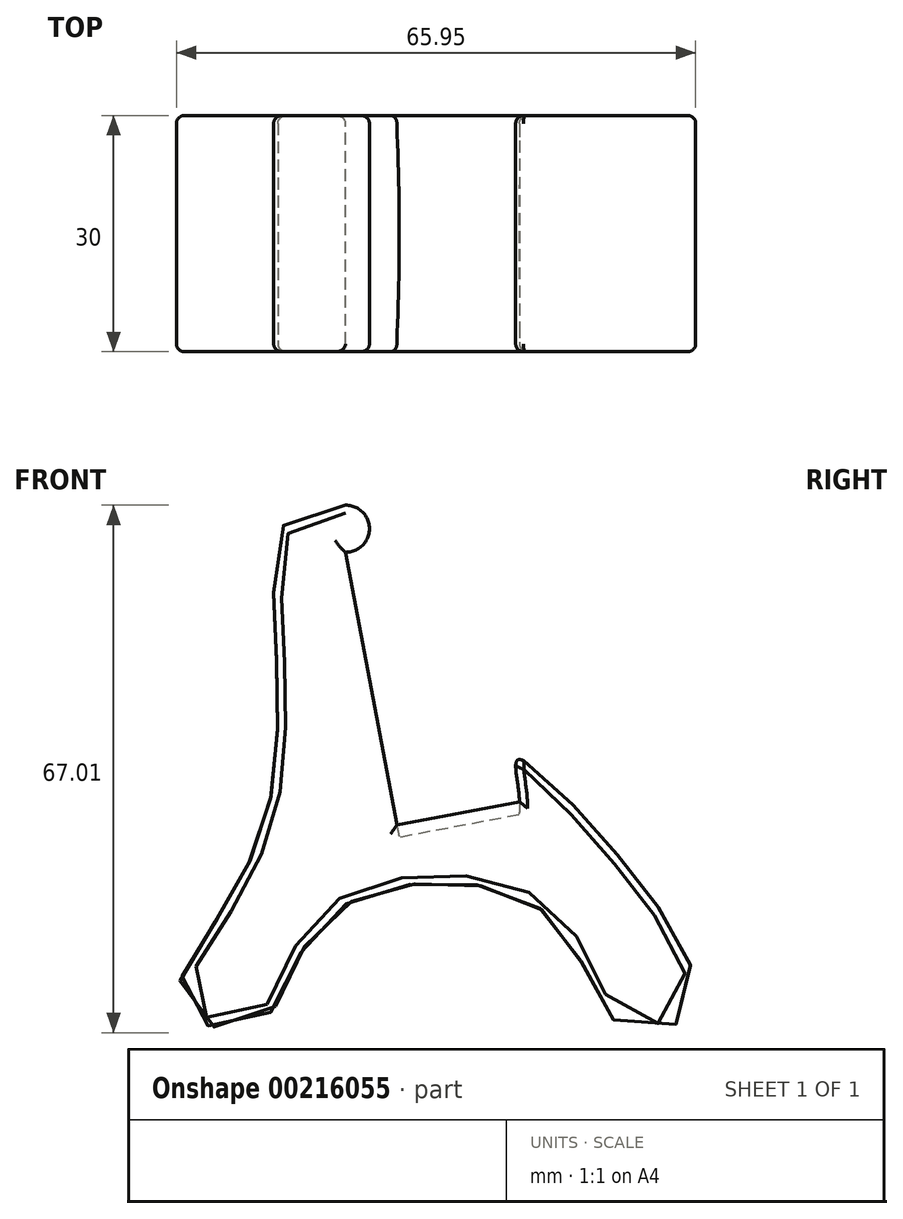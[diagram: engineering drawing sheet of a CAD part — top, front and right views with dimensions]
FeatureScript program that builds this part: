
annotation { "Feature Type Name" : "Feature", "Feature Type Description" : "" }
export const myFeature = defineFeature(function(context is Context, id is Id, definition is map)
    precondition{}
    {
        {
            var Q0;
            Q0=qCreatedBy(makeId("Front.planeOp"),FACE);
            var sketch = newSketch(context, id + "F0", { "sketchPlane" : qUnion([Q0])});
            skLineSegment(sketch, "E0", {"start": v(0, 0) * mm, "end": v(-14.9, -1.77) * mm});
            skLineSegment(sketch, "E1", {"start": v(-14.9, -1.77) * mm, "end": v(-21.73, 34.55) * mm});
            skArc(sketch, "E2", {"start": v(-21.73, 34.55) * mm, "mid": v(-18.7, 37.54) * mm, "end": v(-21.73, 40.53) * mm});
            skFitSpline(sketch, "E3", {"points": [v(-21.73, 40.53) * mm, v(-29.85, 37.54) * mm, v(-32.05, 0) * mm, v(-42.94, -23.18) * mm, v(-32.47, -24.89) * mm, v(-24.14, -11.86) * mm, v(3.42, -11) * mm, v(13.46, -25.74) * mm, v(22.43, -22.97) * mm, v(9.4, 0) * mm, v(0, 8.01) * mm, v(0, 0) * mm], "startDerivative": vector(-163.14, -3.83) * mm, "endDerivative": vector(-51.87, -133.13) * mm});
            skSolve(sketch);
        }
        {
            var Q0;
            Q0 = qSketchRegion(id + "F0", true);
            extrude(context, id + "F1", {"entities" : qUnion([Q0]), "depth" : 30 * mm});
        }
        {
            var Q0;
            Q0=makeQuery(id+"F1.opExtrude","SWEPT_FACE",FACE,{"disambiguationData":[OSD([sQuery(id+"F0.wireOp",EDGE,"E1")])]});
            var sketch = newSketch(context, id + "F2", { "sketchPlane" : qUnion([Q0])});
            skArc(sketch, "E4", {"start": v(-30, 3.01) * mm, "mid": v(-15, 1.1) * mm, "end": v(0, 3.01) * mm});
            skLineSegment(sketch, "E5", {"start": v(-30, 3.01) * mm, "end": v(-30, 1.01) * mm});
            skLineSegment(sketch, "E6", {"start": v(-30, 1.01) * mm, "end": v(0, 1.01) * mm});
            skLineSegment(sketch, "E7", {"start": v(0, 1.01) * mm, "end": v(0, 3.01) * mm});
            skSolve(sketch);
        }
        {
            var Q0;
            Q0 = qSketchRegion(id + "F2", true);
            extrude(context, id + "F3", {"entities" : qUnion([Q0]), "operationType" : NewBodyOperationType.ADD, "depth" : 18 * mm});
        }
        {
            var Q0;
            Q0=makeQuery(id+"F3.opExtrude","SWEPT_FACE",FACE,{"disambiguationData":[OSD([sQuery(id+"F2.wireOp",EDGE,"E6")])]});
            var sketch = newSketch(context, id + "F4", { "sketchPlane" : qUnion([Q0])});
            skLineSegment(sketch, "E8.bottom", {"start": v(-14.97, 30) * mm, "end": v(0, 30) * mm});
            skLineSegment(sketch, "E8.top", {"start": v(-14.97, 0) * mm, "end": v(0, 0) * mm});
            skLineSegment(sketch, "E8.left", {"start": v(-14.97, 30) * mm, "end": v(-14.97, 0) * mm});
            skLineSegment(sketch, "E8.right", {"start": v(0, 30) * mm, "end": v(0, 0) * mm});
            skSolve(sketch);
        }
        {
            var Q0;
            Q0 = qSketchRegion(id + "F4", true);
            extrude(context, id + "F5", {"entities" : qUnion([Q0]), "operationType" : NewBodyOperationType.ADD, "depth" : 3 * mm});
        }
        {
            var Q0;
            Q0=makeQuery(id+"F3.opExtrude","SWEPT_FACE",FACE,{"disambiguationData":[OSD([sQuery(id+"F2.wireOp",EDGE,"E6")])]});
            var sketch = newSketch(context, id + "F6", { "sketchPlane" : qUnion([Q0])});
            skLineSegment(sketch, "E9.bottom", {"start": v(0.48, 30) * mm, "end": v(0, 30) * mm});
            skLineSegment(sketch, "E9.top", {"start": v(0.48, 0) * mm, "end": v(0, 0) * mm});
            skLineSegment(sketch, "E9.left", {"start": v(0.48, 30) * mm, "end": v(0.48, 0) * mm});
            skLineSegment(sketch, "E9.right", {"start": v(0, 30) * mm, "end": v(0, 0) * mm});
            skSolve(sketch);
        }
        {
            var Q0;
            Q0 = qSketchRegion(id + "F6", true);
            extrude(context, id + "F7", {"entities" : qUnion([Q0]), "operationType" : NewBodyOperationType.ADD, "depth" : 2 * mm});
        }
        {
            var Q0;
            Q0=makeQuery(id+"F7.boolean.opBoolean","MERGE",FACE,{"derivedFrom":[makeQuery(id+"F5.boolean.opBoolean","MERGE",FACE,{"derivedFrom":[makeQuery(id+"F3.boolean.opBoolean","MERGE",FACE,{"derivedFrom":[makeQuery(id+"F1.opExtrude","CAP_FACE",FACE,{"disambiguationData":[OSD([sQuery(id+"F0.wireOp",EDGE,"E0"),sQuery(id+"F0.wireOp",EDGE,"E1"),sQuery(id+"F0.wireOp",EDGE,"E2"),sQuery(id+"F0.wireOp",EDGE,"E3")])],"isStart":true}),makeQuery(id+"F3.opExtrude","SWEPT_FACE",FACE,{"disambiguationData":[OSD([sQuery(id+"F2.wireOp",EDGE,"E7")])]})]}),makeQuery(id+"F5.opExtrude","SWEPT_FACE",FACE,{"disambiguationData":[OSD([sQuery(id+"F4.wireOp",EDGE,"E8.top")])]})]}),makeQuery(id+"F7.opExtrude","SWEPT_FACE",FACE,{"disambiguationData":[OSD([sQuery(id+"F6.wireOp",EDGE,"E9.top")])]})]});
            var Q1;
            Q1=makeQuery(id+"F7.boolean.opBoolean","MERGE",FACE,{"derivedFrom":[makeQuery(id+"F5.boolean.opBoolean","MERGE",FACE,{"derivedFrom":[makeQuery(id+"F3.boolean.opBoolean","MERGE",FACE,{"derivedFrom":[makeQuery(id+"F1.opExtrude","CAP_FACE",FACE,{"disambiguationData":[OSD([sQuery(id+"F0.wireOp",EDGE,"E0"),sQuery(id+"F0.wireOp",EDGE,"E1"),sQuery(id+"F0.wireOp",EDGE,"E2"),sQuery(id+"F0.wireOp",EDGE,"E3")])],"isStart":false}),makeQuery(id+"F3.opExtrude","SWEPT_FACE",FACE,{"disambiguationData":[OSD([sQuery(id+"F2.wireOp",EDGE,"E5")])]})]}),makeQuery(id+"F5.opExtrude","SWEPT_FACE",FACE,{"disambiguationData":[OSD([sQuery(id+"F4.wireOp",EDGE,"E8.bottom")])]})]}),makeQuery(id+"F7.opExtrude","SWEPT_FACE",FACE,{"disambiguationData":[OSD([sQuery(id+"F6.wireOp",EDGE,"E9.bottom")])]})]});
            fillet(context, id + "F8", {"entities" : qUnion([Q0, Q1]), "radius" : 1 * mm, "tangentPropagation" : true, "allowEdgeOverflow" : false});
        }
    });
